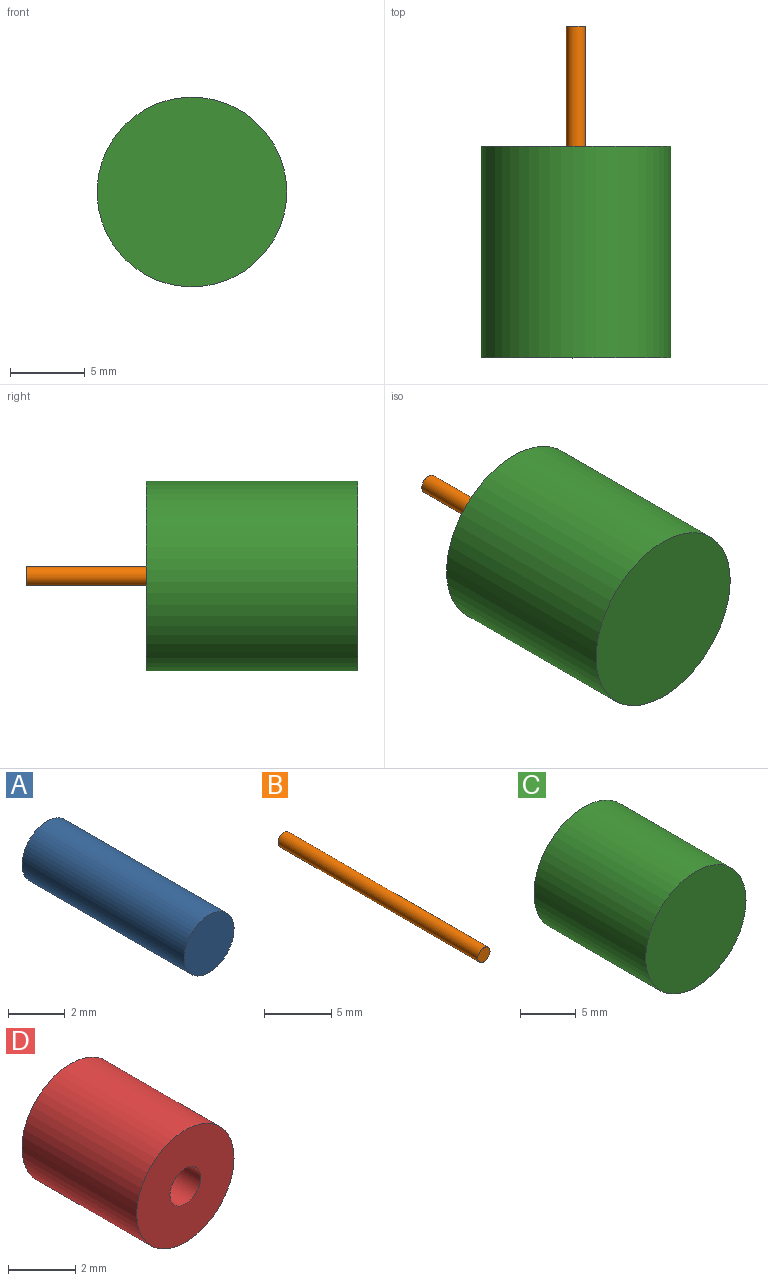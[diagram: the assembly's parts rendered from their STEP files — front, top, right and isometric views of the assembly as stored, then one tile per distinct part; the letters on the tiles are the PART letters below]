
ASSEMBLY  parts=4 mates=3
PART A: 3 faces, bbox 2.5x8.1x2.5 mm
  f0: cylinder r=1.24mm len=8.08mm, axis (0,1,0), area 63.2mm2, adj f1,f2
  f1: plane 2.49x2.49mm, normal (0,-1,0), area 4.9mm2, adj f0
  f2: plane 2.49x2.49mm, normal (0,1,0), area 4.9mm2, adj f0
PART B: 3 faces, bbox 1.3x21x1.3 mm
  f0: cylinder r=0.64mm len=20.96mm, axis (0,1,0), area 83.6mm2, adj f1,f2
  f1: plane 1.27x1.27mm, normal (0,-1,0), area 1.3mm2, adj f0
  f2: plane 1.27x1.27mm, normal (0,1,0), area 1.3mm2, adj f0
PART C: 5 faces, bbox 12.7x14.2x12.7 mm
  f0: cylinder r=2.11mm len=4.83mm, axis (0,1,0), area 63.9mm2, adj f2,f3
  f1: cylinder r=6.35mm len=14.16mm, axis (0,1,0), area 565mm2, adj f2,f4
  f2: plane 12.7x12.7mm, normal (0,1,0), area 112.7mm2, adj f0,f1
  f3: plane 4.22x4.22mm, normal (0,1,0), area 14mm2, adj f0
  f4: plane 12.7x12.7mm, normal (0,-1,0), area 126.7mm2, adj f1
PART D: 4 faces, bbox 4.1x4.8x4.1 mm
  f0: cylinder r=2.04mm len=4.83mm, axis (0,1,0), area 62mm2, adj f1,f2
  f1: plane 4.09x4.09mm, normal (0,-1,0), area 11.8mm2, adj f0,f3
  f2: plane 4.09x4.09mm, normal (0,1,0), area 11.8mm2, adj f0,f3
  f3: cylinder r=0.65mm len=4.83mm, axis (0,-1,0), area 19.6mm2, adj f1,f2
PLACE A t=(-11.16,0.56,-0.12)mm fixed
PLACE B t=(-11.16,8.62,-0.12)mm
PLACE C t=(-11.16,0.56,-0.12)mm fixed
PLACE D rot(axis=(1,0,0),180deg) t=(-11.16,-4.27,-0.12)mm
MATE cylindrical B.f0 <-> C.f0  axis (0,1,0) through (-11.16,8.62,-0.12)mm
MATE cylindrical D.f0 <-> C.f0  axis (0,-1,0) through (-11.16,-4.27,-0.12)mm
MATE fastened D.f0 <-> C.f0  axis (0,1,0) through (-11.16,0.56,-0.12)mm
